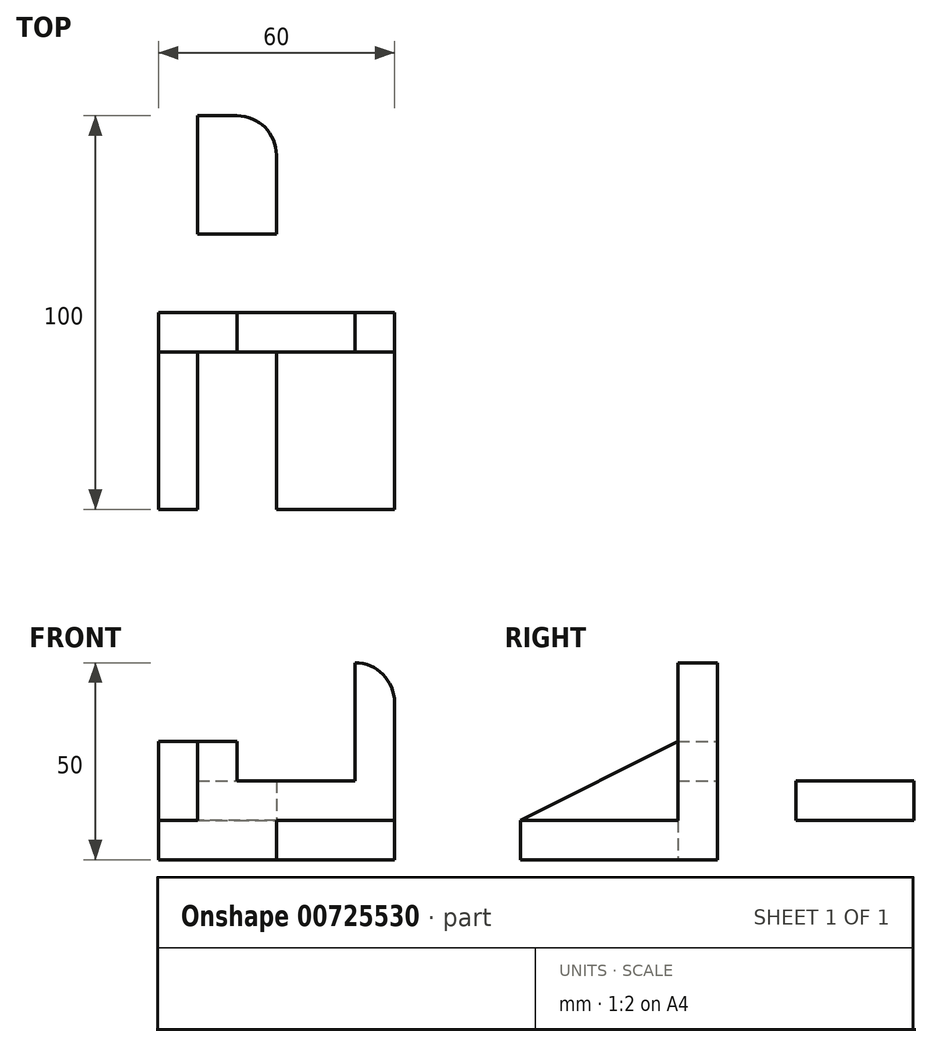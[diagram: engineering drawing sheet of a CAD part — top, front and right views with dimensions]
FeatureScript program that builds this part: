
annotation { "Feature Type Name" : "Feature", "Feature Type Description" : "" }
export const myFeature = defineFeature(function(context is Context, id is Id, definition is map)
    precondition{}
    {
        {
            var Q0;
            Q0=qCreatedBy(makeId("Front.planeOp"),FACE);
            var sketch = newSketch(context, id + "F0", { "sketchPlane" : qUnion([Q0])});
            skLineSegment(sketch, "E0", {"start": v(0, 0) * mm, "end": v(60, 0) * mm});
            skLineSegment(sketch, "E1", {"start": v(0, 0) * mm, "end": v(0, 10) * mm});
            skLineSegment(sketch, "E2", {"start": v(30, 0) * mm, "end": v(60, 0) * mm});
            skLineSegment(sketch, "E3", {"start": v(60, 10) * mm, "end": v(60, 0) * mm});
            skLineSegment(sketch, "E4", {"start": v(0, 10) * mm, "end": v(60, 10) * mm});
            skLineSegment(sketch, "E5", {"start": v(30, 10) * mm, "end": v(30, 0) * mm});
            skLineSegment(sketch, "E6", {"start": v(0, 30) * mm, "end": v(0, 10) * mm});
            skLineSegment(sketch, "E7", {"start": v(0, 30) * mm, "end": v(10, 30) * mm});
            skLineSegment(sketch, "E8", {"start": v(10, 10) * mm, "end": v(10, 30) * mm});
            skLineSegment(sketch, "E9", {"start": v(20, 30) * mm, "end": v(10, 30) * mm});
            skLineSegment(sketch, "E10", {"start": v(20, 20) * mm, "end": v(20, 30) * mm});
            skLineSegment(sketch, "E11", {"start": v(20, 20) * mm, "end": v(50, 20) * mm});
            skLineSegment(sketch, "E12", {"start": v(60, 40) * mm, "end": v(60, 10) * mm});
            skLineSegment(sketch, "E13", {"start": v(50, 50) * mm, "end": v(50, 50) * mm});
            skLineSegment(sketch, "E14", {"start": v(50, 20) * mm, "end": v(50, 50) * mm});
            skPoint(sketch, "E15.visualSharp", {"position": v(60, 50) * mm});
            skArc(sketch, "E15.filletArc", {"start": v(60, 40) * mm, "mid": v(57.07, 47.07) * mm, "end": v(50, 50) * mm});
            skSolve(sketch);
        }
        {
            var Q0;
            {var subQ0=sQuery(id+"F0.wireOp",EDGE,"E6");Q0=makeQuery(id+"F0.imprint","IMPRINT",FACE,{"disambiguationData":[TD([[makeQuery(id+"F0.imprint","IMPRINT",EDGE,{"derivedFrom":subQ0}),1.0]])]});}
            var Q1;
            Q1=makeQuery(id+"F0.imprint","IMPRINT",FACE,{"disambiguationData":[TD([[makeQuery(id+"F0.imprint","IMPRINT",EDGE,{"derivedFrom":sQuery(id+"F0.wireOp",EDGE,"E0")}),1.0]])]});
            extrude(context, id + "F1", {"entities" : qUnion([Q0, Q1]), "depth" : 50 * mm, "offsetDistance" : 25 * mm});
        }
        {
            var Q0;
            Q0=qSketchRegion(id+"F0",true);
            extrude(context, id + "F2", {"entities" : qUnion([Q0]), "operationType" : NewBodyOperationType.ADD, "depth" : 10 * mm, "offsetDistance" : 25 * mm});
        }
        {
            var Q0;
            Q0=makeQuery(id+"F2.opExtrude","CAP_FACE",FACE,{"disambiguationData":[OSD([sQuery(id+"F0.wireOp",EDGE,"E0"),sQuery(id+"F0.wireOp",EDGE,"E1"),sQuery(id+"F0.wireOp",EDGE,"E2"),sQuery(id+"F0.wireOp",EDGE,"E3"),sQuery(id+"F0.wireOp",EDGE,"E6"),sQuery(id+"F0.wireOp",EDGE,"E7"),sQuery(id+"F0.wireOp",EDGE,"E9"),sQuery(id+"F0.wireOp",EDGE,"E10"),sQuery(id+"F0.wireOp",EDGE,"E11"),sQuery(id+"F0.wireOp",EDGE,"E12"),sQuery(id+"F0.wireOp",EDGE,"E14"),sQuery(id+"F0.wireOp",EDGE,"E15.filletArc")])],"isStart":false});
            var sketch = newSketch(context, id + "F3", { "sketchPlane" : qUnion([Q0])});
            skLineSegment(sketch, "E16", {"start": v(30, 10) * mm, "end": v(60, 10) * mm});
            skLineSegment(sketch, "E17", {"start": v(60, 10) * mm, "end": v(30, 10) * mm});
            skLineSegment(sketch, "E18", {"start": v(30, 10) * mm, "end": v(30, 0) * mm});
            skLineSegment(sketch, "E19", {"start": v(30, 0) * mm, "end": v(60, 0) * mm});
            skLineSegment(sketch, "E20", {"start": v(60, 0) * mm, "end": v(60, 10) * mm});
            skSolve(sketch);
        }
        {
            var Q0;
            Q0=makeQuery(id+"FsUGWriKy9odvux_1.boolean.opBoolean","MERGE",FACE,{"derivedFrom":[makeQuery(id+"F1.opExtrude","SWEPT_FACE",FACE,{"disambiguationData":[OSD([sQuery(id+"F0.wireOp",EDGE,"E4")])]}),makeQuery(id+"FsUGWriKy9odvux_1.opExtrude","SWEPT_FACE",FACE,{"disambiguationData":[OSD([sQuery(id+"F3.wireOp",EDGE,"E17")])]})]});
            var sketch = newSketch(context, id + "F4", { "sketchPlane" : qUnion([Q0])});
            skLineSegment(sketch, "E21", {"start": v(60, -10) * mm, "end": v(60, -10) * mm});
            skLineSegment(sketch, "E22", {"start": v(50, -20) * mm, "end": v(30, -20) * mm});
            skLineSegment(sketch, "E23", {"start": v(30, -20) * mm, "end": v(30, -10) * mm});
            skPoint(sketch, "E23.endSnap0", {"position": v(20, -10) * mm});
            skLineSegment(sketch, "E24", {"start": v(30, -10) * mm, "end": v(60, -10) * mm});
            skPoint(sketch, "E25.visualSharp", {"position": v(60, -20) * mm});
            skArc(sketch, "E25.filletArc", {"start": v(50, -20) * mm, "mid": v(57.07, -17.07) * mm, "end": v(60, -10) * mm});
            skSolve(sketch);
        }
        {
            var Q0;
            Q0=makeQuery(id+"F4.imprint","IMPRINT",FACE,{"disambiguationData":[TD([[makeQuery(id+"F4.imprint","IMPRINT",EDGE,{"derivedFrom":sQuery(id+"F4.wireOp",EDGE,"E22")}),-1.0]])]});
            extrude(context, id + "F5", {"entities" : qUnion([Q0]), "operationType" : NewBodyOperationType.ADD, "oppositeDirection" : true, "depth" : 10 * mm, "offsetDistance" : 25 * mm});
        }
        {
            var Q0;
            Q0=makeQuery(id+"F5.boolean.opBoolean","MERGE",FACE,{"derivedFrom":[makeQuery(id+"F1.opExtrude","SWEPT_FACE",FACE,{"disambiguationData":[OSD([sQuery(id+"F0.wireOp",EDGE,"E4")])]}),makeQuery(id+"F5.opExtrude","CAP_FACE",FACE,{"disambiguationData":[OSD([sQuery(id+"F4.wireOp",EDGE,"E22"),sQuery(id+"F4.wireOp",EDGE,"E23"),sQuery(id+"F4.wireOp",EDGE,"E24"),sQuery(id+"F4.wireOp",EDGE,"E25.filletArc")])],"isStart":true})]});
            var sketch = newSketch(context, id + "F6", { "sketchPlane" : qUnion([Q0])});
            skLineSegment(sketch, "E26", {"start": v(10, -50) * mm, "end": v(20, -50) * mm});
            skLineSegment(sketch, "E27", {"start": v(30, -40) * mm, "end": v(30, -20) * mm});
            skLineSegment(sketch, "E28", {"start": v(30, -20) * mm, "end": v(10, -20) * mm});
            skLineSegment(sketch, "E29", {"start": v(10, -20) * mm, "end": v(10, -50) * mm});
            skPoint(sketch, "E30.visualSharp", {"position": v(30, -50) * mm});
            skArc(sketch, "E30.filletArc", {"start": v(20, -50) * mm, "mid": v(27.07, -47.07) * mm, "end": v(30, -40) * mm});
            skLineSegment(sketch, "E31", {"start": v(20, -50) * mm, "end": v(30, -50) * mm});
            skLineSegment(sketch, "E32", {"start": v(30, -40) * mm, "end": v(30, -50) * mm});
            skSolve(sketch);
        }
        {
            var Q0;
            Q0=qSketchRegion(id+"F6",true);
            extrude(context, id + "F7", {"entities" : qUnion([Q0]), "operationType" : NewBodyOperationType.ADD, "oppositeDirection" : true, "depth" : 10 * mm, "offsetDistance" : 25 * mm});
        }
        {
            var Q0;
            Q0=makeQuery(id+"F5.boolean.opBoolean","MERGE",FACE,{"derivedFrom":[makeQuery(id+"F1.opExtrude","SWEPT_FACE",FACE,{"disambiguationData":[OSD([sQuery(id+"F0.wireOp",EDGE,"E4")])]}),makeQuery(id+"F5.opExtrude","CAP_FACE",FACE,{"disambiguationData":[OSD([sQuery(id+"F4.wireOp",EDGE,"E22"),sQuery(id+"F4.wireOp",EDGE,"E23"),sQuery(id+"F4.wireOp",EDGE,"E24"),sQuery(id+"F4.wireOp",EDGE,"E25.filletArc")])],"isStart":true})]});
            var sketch = newSketch(context, id + "F8", { "sketchPlane" : qUnion([Q0])});
            skLineSegment(sketch, "E33", {"start": v(30, -50) * mm, "end": v(20, -50) * mm});
            skLineSegment(sketch, "E34", {"start": v(30, -40) * mm, "end": v(30, -50) * mm});
            skArc(sketch, "E35", {"start": v(20, -50) * mm, "mid": v(27.07, -47.07) * mm, "end": v(30, -40) * mm});
            skSolve(sketch);
        }
        {
            var Q0;
            Q0=qSketchRegion(id+"F8",true);
            extrude(context, id + "F9", {"entities" : qUnion([Q0]), "operationType" : NewBodyOperationType.REMOVE, "oppositeDirection" : true, "depth" : 25 * mm, "offsetDistance" : 25 * mm});
        }
        {
            var Q0;
            Q0=makeQuery(id+"F1.opExtrude","SWEPT_FACE",FACE,{"disambiguationData":[OSD([sQuery(id+"F0.wireOp",EDGE,"E8")])]});
            var sketch = newSketch(context, id + "F10", { "sketchPlane" : qUnion([Q0])});
            skLineSegment(sketch, "E36", {"start": v(-10, 30) * mm, "end": v(-50, 10) * mm});
            skLineSegment(sketch, "E37", {"start": v(-50, 10) * mm, "end": v(-50, 30) * mm});
            skLineSegment(sketch, "E38", {"start": v(-50, 30) * mm, "end": v(-10, 30) * mm});
            skSolve(sketch);
        }
        {
            var Q0;
            Q0=makeQuery(id+"F10.imprint","IMPRINT",FACE,{"disambiguationData":[TD([[makeQuery(id+"F10.imprint","IMPRINT",EDGE,{"derivedFrom":sQuery(id+"F10.wireOp",EDGE,"E36")}),-1.0]])]});
            extrude(context, id + "F11", {"entities" : qUnion([Q0]), "operationType" : NewBodyOperationType.REMOVE, "oppositeDirection" : true, "depth" : 25 * mm, "offsetDistance" : 25 * mm});
        }
    });
